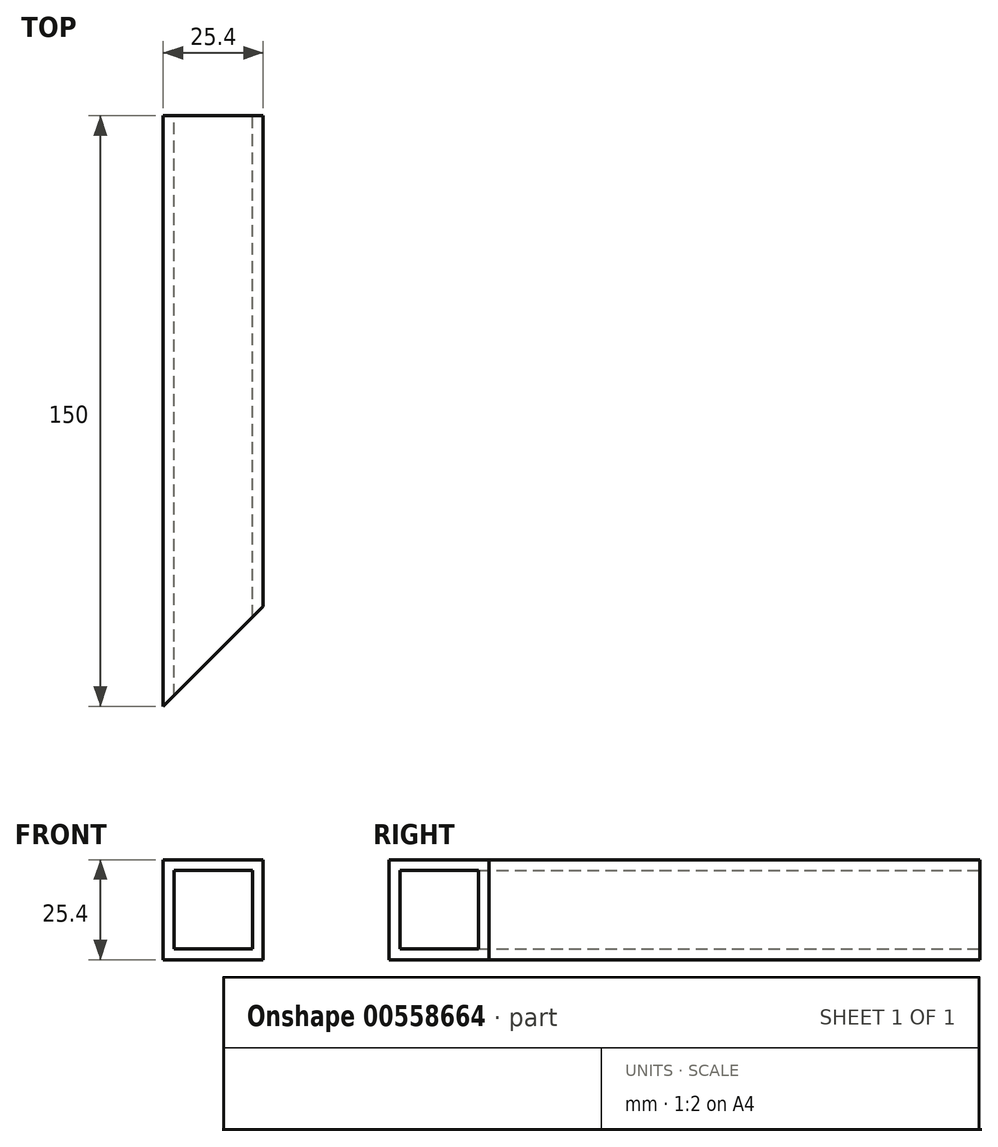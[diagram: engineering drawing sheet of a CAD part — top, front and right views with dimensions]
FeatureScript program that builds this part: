
annotation { "Feature Type Name" : "Feature", "Feature Type Description" : "" }
export const myFeature = defineFeature(function(context is Context, id is Id, definition is map)
    precondition{}
    {
        {
            var Q0;
            Q0=qCreatedBy(makeId("Front.planeOp"),FACE);
            var sketch = newSketch(context, id + "F0", { "sketchPlane" : qUnion([Q0])});
            skLineSegment(sketch, "E0.bottom", {"start": v(-12.7, -12.7) * mm, "end": v(12.7, -12.7) * mm});
            skLineSegment(sketch, "E0.top", {"start": v(-12.7, 12.7) * mm, "end": v(12.7, 12.7) * mm});
            skLineSegment(sketch, "E0.left", {"start": v(-12.7, -12.7) * mm, "end": v(-12.7, 12.7) * mm});
            skLineSegment(sketch, "E0.right", {"start": v(12.7, -12.7) * mm, "end": v(12.7, 12.7) * mm});
            skPoint(sketch, "E0.middle", {"position": v(0, 0) * mm});
            skLineSegment(sketch, "E1.bottom", {"start": v(-10, -10) * mm, "end": v(10, -10) * mm});
            skLineSegment(sketch, "E1.top", {"start": v(-10, 10) * mm, "end": v(10, 10) * mm});
            skLineSegment(sketch, "E1.left", {"start": v(-10, -10) * mm, "end": v(-10, 10) * mm});
            skLineSegment(sketch, "E1.right", {"start": v(10, -10) * mm, "end": v(10, 10) * mm});
            skSolve(sketch);
        }
        {
            var Q0;
            Q0=makeQuery(id+"F0.imprint","IMPRINT",FACE,{"disambiguationData":[TD([[makeQuery(id+"F0.imprint","IMPRINT",EDGE,{"derivedFrom":sQuery(id+"F0.wireOp",EDGE,"E0.bottom")}),1.0]])]});
            extrude(context, id + "F1", {"entities" : qUnion([Q0]), "depth" : 150 * mm, "offsetDistance" : 25 * mm});
        }
        {
            var Q0;
            Q0=makeQuery(id+"F1.opExtrude","SWEPT_FACE",FACE,{"disambiguationData":[OSD([sQuery(id+"F0.wireOp",EDGE,"E0.top")])]});
            var sketch = newSketch(context, id + "F2", { "sketchPlane" : qUnion([Q0])});
            skLineSegment(sketch, "E2", {"start": v(-12.7, 0) * mm, "end": v(12.7, -25.4) * mm});
            skLineSegment(sketch, "E3", {"start": v(-12.7, -150) * mm, "end": v(12.7, -124.6) * mm});
            skSolve(sketch);
        }
        {
            var Q0;
            {var subQ0=sQuery(id+"F2.wireOp",EDGE,"E3");Q0=makeQuery(id+"F2.imprint","IMPRINT",FACE,{"disambiguationData":[TD([[makeQuery(id+"F2.imprint","IMPRINT",EDGE,{"derivedFrom":subQ0}),-1.0]])]});}
            extrude(context, id + "F3", {"entities" : qUnion([Q0]), "operationType" : NewBodyOperationType.REMOVE, "oppositeDirection" : true, "depth" : 200 * mm, "offsetDistance" : 25 * mm});
        }
    });
